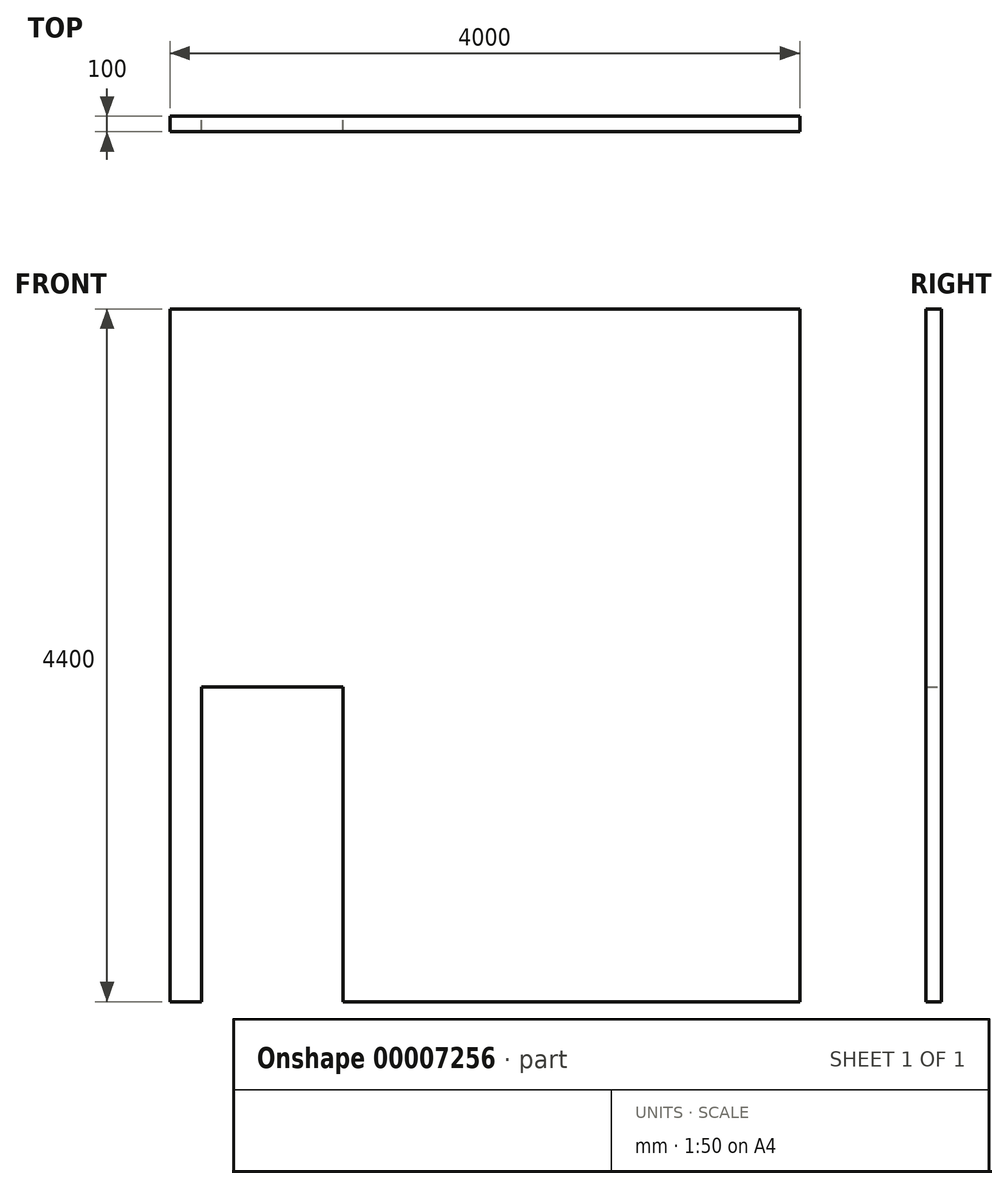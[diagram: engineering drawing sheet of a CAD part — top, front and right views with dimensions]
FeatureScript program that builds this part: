
annotation { "Feature Type Name" : "Feature", "Feature Type Description" : "" }
export const myFeature = defineFeature(function(context is Context, id is Id, definition is map)
    precondition{}
    {
        {
            var Q0;
            Q0=qCreatedBy(makeId("Front.planeOp"),FACE);
            var sketch = newSketch(context, id + "F0", { "sketchPlane" : qUnion([Q0])});
            skLineSegment(sketch, "E0", {"start": v(0, 0) * mm, "end": v(0, 4400) * mm});
            skLineSegment(sketch, "E1", {"start": v(0, 4400) * mm, "end": v(4000, 4400) * mm});
            skLineSegment(sketch, "E2", {"start": v(4000, 4400) * mm, "end": v(4000, 0) * mm});
            skLineSegment(sketch, "E3", {"start": v(4000, 0) * mm, "end": v(1100, 0) * mm});
            skLineSegment(sketch, "E4", {"start": v(1100, 0) * mm, "end": v(1100, 2000) * mm});
            skLineSegment(sketch, "E5", {"start": v(1100, 2000) * mm, "end": v(200, 2000) * mm});
            skLineSegment(sketch, "E6", {"start": v(200, 2000) * mm, "end": v(200, 0) * mm});
            skLineSegment(sketch, "E7", {"start": v(200, 0) * mm, "end": v(0, 0) * mm});
            skSolve(sketch);
        }
        {
            var Q0;
            Q0=makeQuery(id+"F0.imprint","IMPRINT",FACE,{"disambiguationData":[TD([[makeQuery(id+"F0.imprint","IMPRINT",EDGE,{"derivedFrom":sQuery(id+"F0.wireOp",EDGE,"E0")}),-1.0]])]});
            extrude(context, id + "F1", {"entities" : qUnion([Q0]), "depth" : 100 * mm});
        }
    });
